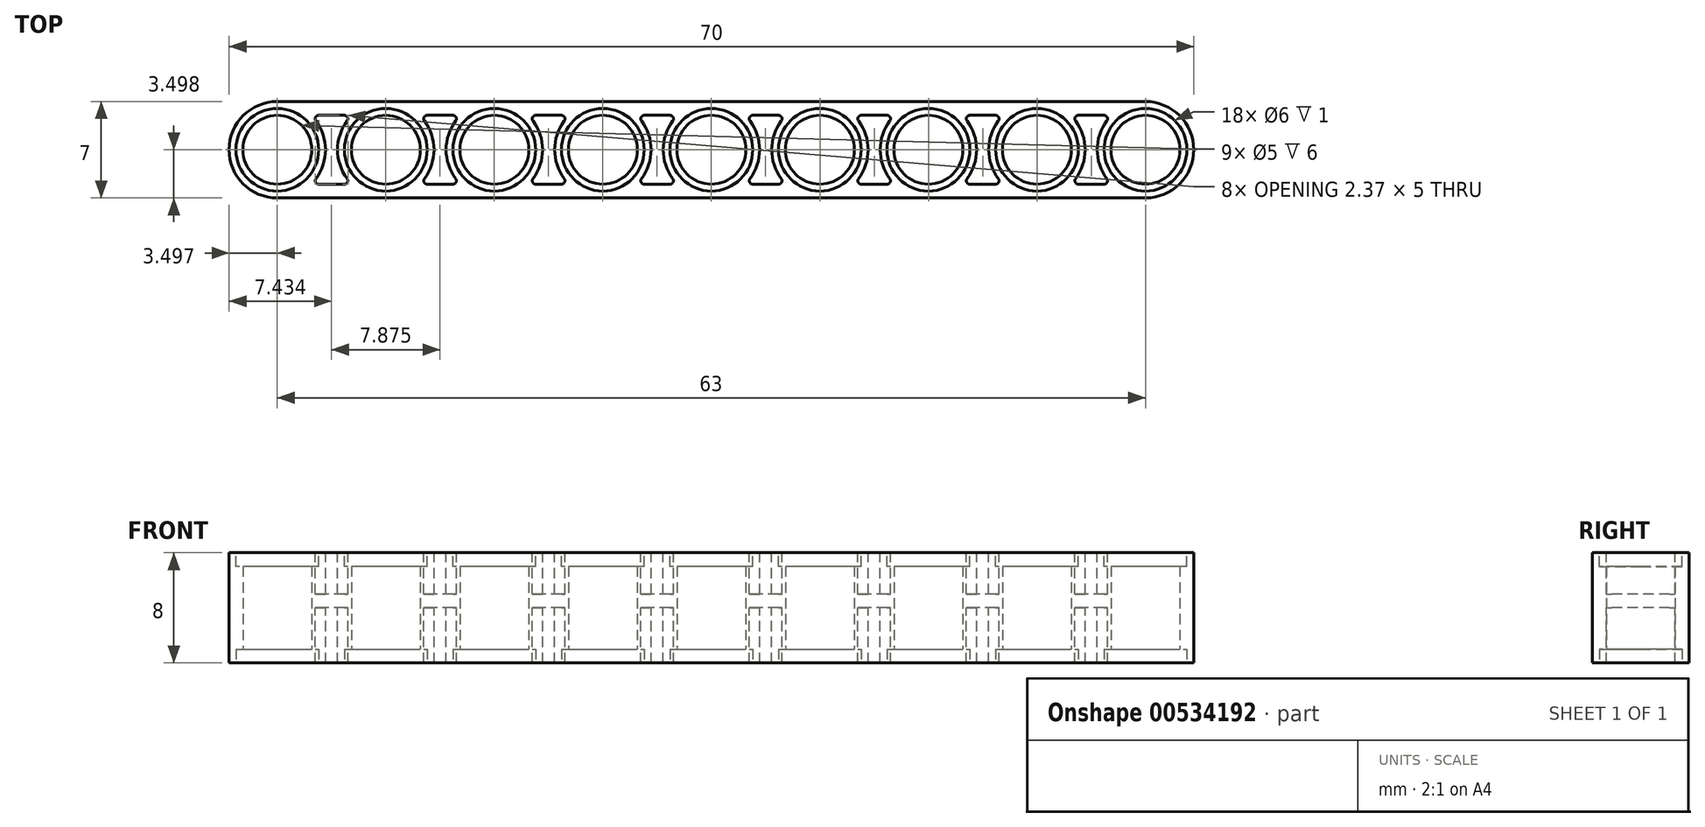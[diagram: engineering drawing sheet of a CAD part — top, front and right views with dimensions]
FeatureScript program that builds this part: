
annotation { "Feature Type Name" : "Feature", "Feature Type Description" : "" }
export const myFeature = defineFeature(function(context is Context, id is Id, definition is map)
    precondition{}
    {
        {
            var Q0;
            Q0=qCreatedBy(makeId("Top.planeOp"),FACE);
            var sketch = newSketch(context, id + "F0", { "sketchPlane" : qUnion([Q0])});
            skCircle(sketch, "E0", {"center": v(-40.67, -41.82) * mm, "radius": 3.5 * mm});
            skLineSegment(sketch, "E1", {"start": v(-40.67, -41.82) * mm, "end": v(22.33, -41.82) * mm});
            skCircle(sketch, "E2", {"center": v(22.33, -41.82) * mm, "radius": 3.5 * mm});
            skLineSegment(sketch, "E3", {"start": v(22.33, -45.32) * mm, "end": v(-40.67, -45.32) * mm});
            skLineSegment(sketch, "E4", {"start": v(-40.67, -38.32) * mm, "end": v(22.33, -38.32) * mm});
            skSolve(sketch);
        }
        {
            var Q0;
            Q0=qSketchRegion(id+"F0",true);
            extrude(context, id + "F1", {"entities" : qUnion([Q0]), "depth" : 8 * mm, "offsetDistance" : 25 * mm});
        }
        {
            var Q0;
            Q0=makeQuery(id+"F1.opExtrude","CAP_FACE",FACE,{"disambiguationData":[OSD([sQuery(id+"F0.wireOp",EDGE,"E0"),sQuery(id+"F0.wireOp",EDGE,"E2"),sQuery(id+"F0.wireOp",EDGE,"E3"),sQuery(id+"F0.wireOp",EDGE,"E4")])],"isStart":true});
            var sketch = newSketch(context, id + "F2", { "sketchPlane" : qUnion([Q0])});
            skArc(sketch, "E5.0", {"start": v(-40.71, -42.4) * mm, "mid": v(-38.21, -39.9) * mm, "end": v(-40.71, -37.4) * mm});
            skArc(sketch, "E5.1", {"start": v(-40.71, -37.4) * mm, "mid": v(-43.21, -39.9) * mm, "end": v(-40.71, -42.4) * mm});
            skCircle(sketch, "E6.0", {"center": v(-40.71, -39.9) * mm, "radius": 3 * mm});
            skLineSegment(sketch, "E7", {"start": v(-38.26, -42.4) * mm, "end": v(-35.16, -42.4) * mm});
            skLineSegment(sketch, "E8", {"start": v(-38.26, -37.4) * mm, "end": v(-35.16, -37.4) * mm});
            skArc(sketch, "E9", {"start": v(-35.16, -37.4) * mm, "mid": v(-36.21, -39.9) * mm, "end": v(-35.16, -42.4) * mm});
            skArc(sketch, "E10", {"start": v(-38.26, -42.4) * mm, "mid": v(-37.21, -39.9) * mm, "end": v(-38.26, -37.4) * mm});
            skCircle(sketch, "E11", {"center": v(-40.67, 41.82) * mm, "radius": 3 * mm});
            skCircle(sketch, "E12", {"center": v(-40.67, 41.82) * mm, "radius": 2.5 * mm});
            skCircle(sketch, "E13.1.0.0", {"center": v(-32.8, 41.82) * mm, "radius": 2.5 * mm});
            skCircle(sketch, "E13.1.0.1", {"center": v(-32.8, 41.82) * mm, "radius": 3 * mm});
            skCircle(sketch, "E13.2.0.0", {"center": v(-24.92, 41.82) * mm, "radius": 2.5 * mm});
            skCircle(sketch, "E13.2.0.1", {"center": v(-24.92, 41.82) * mm, "radius": 3 * mm});
            skCircle(sketch, "E13.3.0.0", {"center": v(-17.05, 41.82) * mm, "radius": 2.5 * mm});
            skCircle(sketch, "E13.3.0.1", {"center": v(-17.05, 41.82) * mm, "radius": 3 * mm});
            skCircle(sketch, "E13.4.0.0", {"center": v(-9.17, 41.82) * mm, "radius": 2.5 * mm});
            skCircle(sketch, "E13.4.0.1", {"center": v(-9.17, 41.82) * mm, "radius": 3 * mm});
            skCircle(sketch, "E13.5.0.0", {"center": v(-1.3, 41.82) * mm, "radius": 2.5 * mm});
            skCircle(sketch, "E13.5.0.1", {"center": v(-1.3, 41.82) * mm, "radius": 3 * mm});
            skCircle(sketch, "E13.6.0.0", {"center": v(6.58, 41.82) * mm, "radius": 2.5 * mm});
            skCircle(sketch, "E13.6.0.1", {"center": v(6.58, 41.82) * mm, "radius": 3 * mm});
            skCircle(sketch, "E13.7.0.0", {"center": v(14.45, 41.82) * mm, "radius": 2.5 * mm});
            skCircle(sketch, "E13.7.0.1", {"center": v(14.45, 41.82) * mm, "radius": 3 * mm});
            skCircle(sketch, "E13.8.0.0", {"center": v(22.33, 41.82) * mm, "radius": 2.5 * mm});
            skCircle(sketch, "E13.8.0.1", {"center": v(22.33, 41.82) * mm, "radius": 3 * mm});
            skLineSegment(sketch, "E13.direction1", {"start": v(-40.67, 41.82) * mm, "end": v(-32.8, 41.82) * mm, "construction": true});
            skSolve(sketch);
        }
        {
            var Q0;
            Q0=makeQuery(id+"F2.imprint","IMPRINT",FACE,{"disambiguationData":[TD([[makeQuery(id+"F2.imprint","IMPRINT",EDGE,{"derivedFrom":sQuery(id+"F2.wireOp",EDGE,"E12")}),1.0]])]});
            var Q1;
            Q1=makeQuery(id+"F2.imprint","IMPRINT",FACE,{"disambiguationData":[TD([[makeQuery(id+"F2.imprint","IMPRINT",EDGE,{"derivedFrom":sQuery(id+"F2.wireOp",EDGE,"E13.1.0.0")}),1.0]])]});
            var Q2;
            Q2=makeQuery(id+"F2.imprint","IMPRINT",FACE,{"disambiguationData":[TD([[makeQuery(id+"F2.imprint","IMPRINT",EDGE,{"derivedFrom":sQuery(id+"F2.wireOp",EDGE,"E13.2.0.0")}),1.0]])]});
            var Q3;
            Q3=makeQuery(id+"F2.imprint","IMPRINT",FACE,{"disambiguationData":[TD([[makeQuery(id+"F2.imprint","IMPRINT",EDGE,{"derivedFrom":sQuery(id+"F2.wireOp",EDGE,"E13.3.0.0")}),1.0]])]});
            var Q4;
            Q4=makeQuery(id+"F2.imprint","IMPRINT",FACE,{"disambiguationData":[TD([[makeQuery(id+"F2.imprint","IMPRINT",EDGE,{"derivedFrom":sQuery(id+"F2.wireOp",EDGE,"E13.4.0.0")}),1.0]])]});
            var Q5;
            Q5=makeQuery(id+"F2.imprint","IMPRINT",FACE,{"disambiguationData":[TD([[makeQuery(id+"F2.imprint","IMPRINT",EDGE,{"derivedFrom":sQuery(id+"F2.wireOp",EDGE,"E13.5.0.0")}),1.0]])]});
            var Q6;
            Q6=makeQuery(id+"F2.imprint","IMPRINT",FACE,{"disambiguationData":[TD([[makeQuery(id+"F2.imprint","IMPRINT",EDGE,{"derivedFrom":sQuery(id+"F2.wireOp",EDGE,"E13.6.0.0")}),1.0]])]});
            var Q7;
            Q7=makeQuery(id+"F2.imprint","IMPRINT",FACE,{"disambiguationData":[TD([[makeQuery(id+"F2.imprint","IMPRINT",EDGE,{"derivedFrom":sQuery(id+"F2.wireOp",EDGE,"E13.7.0.0")}),1.0]])]});
            var Q8;
            Q8=makeQuery(id+"F2.imprint","IMPRINT",FACE,{"disambiguationData":[TD([[makeQuery(id+"F2.imprint","IMPRINT",EDGE,{"derivedFrom":sQuery(id+"F2.wireOp",EDGE,"E13.8.0.0")}),1.0]])]});
            var Q9;
            Q9 = qSketchRegion(id + "F5", true);
            extrude(context, id + "F3", {"entities" : qUnion([Q0, Q1, Q2, Q3, Q4, Q5, Q6, Q7, Q8, Q9]), "operationType" : NewBodyOperationType.REMOVE, "oppositeDirection" : true, "depth" : 25 * mm, "offsetDistance" : 25 * mm});
        }
        {
            var Q0;
            Q0=makeQuery(id+"F2.imprint","IMPRINT",FACE,{"disambiguationData":[TD([[makeQuery(id+"F2.imprint","IMPRINT",EDGE,{"derivedFrom":sQuery(id+"F2.wireOp",EDGE,"E11")}),1.0]])]});
            var Q1;
            Q1=makeQuery(id+"F2.imprint","IMPRINT",FACE,{"disambiguationData":[TD([[makeQuery(id+"F2.imprint","IMPRINT",EDGE,{"derivedFrom":sQuery(id+"F2.wireOp",EDGE,"E13.1.0.0")}),-1.0]])]});
            var Q2;
            Q2=makeQuery(id+"F2.imprint","IMPRINT",FACE,{"disambiguationData":[TD([[makeQuery(id+"F2.imprint","IMPRINT",EDGE,{"derivedFrom":sQuery(id+"F2.wireOp",EDGE,"E13.2.0.0")}),-1.0]])]});
            var Q3;
            Q3=makeQuery(id+"F2.imprint","IMPRINT",FACE,{"disambiguationData":[TD([[makeQuery(id+"F2.imprint","IMPRINT",EDGE,{"derivedFrom":sQuery(id+"F2.wireOp",EDGE,"E13.3.0.0")}),-1.0]])]});
            var Q4;
            Q4=makeQuery(id+"F2.imprint","IMPRINT",FACE,{"disambiguationData":[TD([[makeQuery(id+"F2.imprint","IMPRINT",EDGE,{"derivedFrom":sQuery(id+"F2.wireOp",EDGE,"E13.4.0.0")}),-1.0]])]});
            var Q5;
            Q5=makeQuery(id+"F2.imprint","IMPRINT",FACE,{"disambiguationData":[TD([[makeQuery(id+"F2.imprint","IMPRINT",EDGE,{"derivedFrom":sQuery(id+"F2.wireOp",EDGE,"E13.5.0.0")}),-1.0]])]});
            var Q6;
            Q6=makeQuery(id+"F2.imprint","IMPRINT",FACE,{"disambiguationData":[TD([[makeQuery(id+"F2.imprint","IMPRINT",EDGE,{"derivedFrom":sQuery(id+"F2.wireOp",EDGE,"E13.6.0.0")}),-1.0]])]});
            var Q7;
            Q7=makeQuery(id+"F2.imprint","IMPRINT",FACE,{"disambiguationData":[TD([[makeQuery(id+"F2.imprint","IMPRINT",EDGE,{"derivedFrom":sQuery(id+"F2.wireOp",EDGE,"E13.7.0.0")}),-1.0]])]});
            var Q8;
            Q8=makeQuery(id+"F2.imprint","IMPRINT",FACE,{"disambiguationData":[TD([[makeQuery(id+"F2.imprint","IMPRINT",EDGE,{"derivedFrom":sQuery(id+"F2.wireOp",EDGE,"E13.8.0.0")}),-1.0]])]});
            extrude(context, id + "F4", {"entities" : qUnion([Q0, Q1, Q2, Q3, Q4, Q5, Q6, Q7, Q8]), "operationType" : NewBodyOperationType.REMOVE, "oppositeDirection" : true, "depth" : 1 * mm, "offsetDistance" : 25 * mm});
        }
        {
            var Q0;
            Q0=makeQuery(id+"F1.opExtrude","CAP_FACE",FACE,{"disambiguationData":[OSD([sQuery(id+"F0.wireOp",EDGE,"E0"),sQuery(id+"F0.wireOp",EDGE,"E2"),sQuery(id+"F0.wireOp",EDGE,"E3"),sQuery(id+"F0.wireOp",EDGE,"E4")])],"isStart":false});
            var sketch = newSketch(context, id + "F5", { "sketchPlane" : qUnion([Q0])});
            skCircle(sketch, "E14", {"center": v(22.33, -41.82) * mm, "radius": 3 * mm});
            skCircle(sketch, "E15.1.0.0", {"center": v(14.45, -41.82) * mm, "radius": 3 * mm});
            skCircle(sketch, "E15.2.0.0", {"center": v(6.58, -41.82) * mm, "radius": 3 * mm});
            skCircle(sketch, "E15.3.0.0", {"center": v(-1.3, -41.82) * mm, "radius": 3 * mm});
            skCircle(sketch, "E15.4.0.0", {"center": v(-9.17, -41.82) * mm, "radius": 3 * mm});
            skCircle(sketch, "E15.5.0.0", {"center": v(-17.05, -41.82) * mm, "radius": 3 * mm});
            skCircle(sketch, "E15.6.0.0", {"center": v(-24.92, -41.82) * mm, "radius": 3 * mm});
            skCircle(sketch, "E15.7.0.0", {"center": v(-32.8, -41.82) * mm, "radius": 3 * mm});
            skCircle(sketch, "E15.8.0.0", {"center": v(-40.67, -41.82) * mm, "radius": 3 * mm});
            skLineSegment(sketch, "E15.direction1", {"start": v(22.33, -41.82) * mm, "end": v(14.45, -41.82) * mm, "construction": true});
            skSolve(sketch);
        }
        {
            var Q0;
            Q0=makeQuery(id+"F5.imprint","IMPRINT",FACE,{"disambiguationData":[TD([[makeQuery(id+"F5.imprint","IMPRINT",EDGE,{"derivedFrom":sQuery(id+"F5.wireOp",EDGE,"E14")}),1.0]])]});
            var Q1;
            Q1=makeQuery(id+"F5.imprint","IMPRINT",FACE,{"disambiguationData":[TD([[makeQuery(id+"F5.imprint","IMPRINT",EDGE,{"derivedFrom":sQuery(id+"F5.wireOp",EDGE,"E15.1.0.0")}),1.0]])]});
            var Q2;
            Q2=makeQuery(id+"F5.imprint","IMPRINT",FACE,{"disambiguationData":[TD([[makeQuery(id+"F5.imprint","IMPRINT",EDGE,{"derivedFrom":sQuery(id+"F5.wireOp",EDGE,"E15.2.0.0")}),1.0]])]});
            var Q3;
            Q3=makeQuery(id+"F5.imprint","IMPRINT",FACE,{"disambiguationData":[TD([[makeQuery(id+"F5.imprint","IMPRINT",EDGE,{"derivedFrom":sQuery(id+"F5.wireOp",EDGE,"E15.3.0.0")}),1.0]])]});
            var Q4;
            Q4=makeQuery(id+"F5.imprint","IMPRINT",FACE,{"disambiguationData":[TD([[makeQuery(id+"F5.imprint","IMPRINT",EDGE,{"derivedFrom":sQuery(id+"F5.wireOp",EDGE,"E15.4.0.0")}),1.0]])]});
            var Q5;
            Q5=makeQuery(id+"F5.imprint","IMPRINT",FACE,{"disambiguationData":[TD([[makeQuery(id+"F5.imprint","IMPRINT",EDGE,{"derivedFrom":sQuery(id+"F5.wireOp",EDGE,"E15.5.0.0")}),1.0]])]});
            var Q6;
            Q6=makeQuery(id+"F5.imprint","IMPRINT",FACE,{"disambiguationData":[TD([[makeQuery(id+"F5.imprint","IMPRINT",EDGE,{"derivedFrom":sQuery(id+"F5.wireOp",EDGE,"E15.6.0.0")}),1.0]])]});
            var Q7;
            Q7=makeQuery(id+"F5.imprint","IMPRINT",FACE,{"disambiguationData":[TD([[makeQuery(id+"F5.imprint","IMPRINT",EDGE,{"derivedFrom":sQuery(id+"F5.wireOp",EDGE,"E15.7.0.0")}),1.0]])]});
            var Q8;
            Q8=makeQuery(id+"F5.imprint","IMPRINT",FACE,{"disambiguationData":[TD([[makeQuery(id+"F5.imprint","IMPRINT",EDGE,{"derivedFrom":sQuery(id+"F5.wireOp",EDGE,"E15.8.0.0")}),1.0]])]});
            extrude(context, id + "F6", {"entities" : qUnion([Q0, Q1, Q2, Q3, Q4, Q5, Q6, Q7, Q8]), "operationType" : NewBodyOperationType.REMOVE, "oppositeDirection" : true, "depth" : 1 * mm, "offsetDistance" : 25 * mm});
        }
        {
            var Q0;
            Q0=makeQuery(id+"F1.opExtrude","CAP_FACE",FACE,{"disambiguationData":[OSD([sQuery(id+"F0.wireOp",EDGE,"E0"),sQuery(id+"F0.wireOp",EDGE,"E2"),sQuery(id+"F0.wireOp",EDGE,"E3"),sQuery(id+"F0.wireOp",EDGE,"E4")])],"isStart":false});
            var sketch = newSketch(context, id + "F7", { "sketchPlane" : qUnion([Q0])});
            skArc(sketch, "E16", {"start": v(19.52, -39.73) * mm, "mid": v(18.83, -41.82) * mm, "end": v(19.52, -43.92) * mm});
            skArc(sketch, "E17", {"start": v(17.25, -43.92) * mm, "mid": v(17.95, -41.82) * mm, "end": v(17.25, -39.73) * mm});
            skLineSegment(sketch, "E18", {"start": v(19.32, -44.32) * mm, "end": v(17.46, -44.32) * mm});
            skLineSegment(sketch, "E19", {"start": v(19.32, -39.32) * mm, "end": v(17.46, -39.32) * mm});
            skPoint(sketch, "E20.visualSharp", {"position": v(19.88, -44.32) * mm});
            skArc(sketch, "E20.filletArc", {"start": v(19.32, -44.32) * mm, "mid": v(19.55, -44.18) * mm, "end": v(19.52, -43.92) * mm});
            skPoint(sketch, "E21.visualSharp", {"position": v(16.9, -44.32) * mm});
            skArc(sketch, "E21.filletArc", {"start": v(17.25, -43.92) * mm, "mid": v(17.23, -44.18) * mm, "end": v(17.46, -44.32) * mm});
            skPoint(sketch, "E22.visualSharp", {"position": v(19.88, -39.32) * mm});
            skArc(sketch, "E22.filletArc", {"start": v(19.52, -39.73) * mm, "mid": v(19.55, -39.46) * mm, "end": v(19.32, -39.32) * mm});
            skPoint(sketch, "E23.visualSharp", {"position": v(16.9, -39.32) * mm});
            skArc(sketch, "E23.filletArc", {"start": v(17.46, -39.32) * mm, "mid": v(17.23, -39.46) * mm, "end": v(17.25, -39.73) * mm});
            skArc(sketch, "E24.1.0.0", {"start": v(11.65, -39.73) * mm, "mid": v(10.95, -41.82) * mm, "end": v(11.65, -43.92) * mm});
            skArc(sketch, "E24.1.0.1", {"start": v(9.38, -43.92) * mm, "mid": v(10.08, -41.82) * mm, "end": v(9.38, -39.73) * mm});
            skLineSegment(sketch, "E24.1.0.2", {"start": v(11.45, -44.32) * mm, "end": v(9.58, -44.32) * mm});
            skArc(sketch, "E24.1.0.3", {"start": v(11.45, -44.32) * mm, "mid": v(11.67, -44.18) * mm, "end": v(11.65, -43.92) * mm});
            skArc(sketch, "E24.1.0.4", {"start": v(9.38, -43.92) * mm, "mid": v(9.36, -44.18) * mm, "end": v(9.58, -44.32) * mm});
            skArc(sketch, "E24.1.0.5", {"start": v(9.58, -39.32) * mm, "mid": v(9.36, -39.46) * mm, "end": v(9.38, -39.73) * mm});
            skLineSegment(sketch, "E24.1.0.6", {"start": v(11.45, -39.32) * mm, "end": v(9.58, -39.32) * mm});
            skArc(sketch, "E24.1.0.7", {"start": v(11.65, -39.73) * mm, "mid": v(11.67, -39.46) * mm, "end": v(11.45, -39.32) * mm});
            skArc(sketch, "E24.2.0.0", {"start": v(3.77, -39.73) * mm, "mid": v(3.08, -41.82) * mm, "end": v(3.77, -43.92) * mm});
            skArc(sketch, "E24.2.0.1", {"start": v(1.5, -43.92) * mm, "mid": v(2.2, -41.82) * mm, "end": v(1.5, -39.73) * mm});
            skLineSegment(sketch, "E24.2.0.2", {"start": v(3.57, -44.32) * mm, "end": v(1.7, -44.32) * mm});
            skArc(sketch, "E24.2.0.3", {"start": v(3.57, -44.32) * mm, "mid": v(3.8, -44.18) * mm, "end": v(3.77, -43.92) * mm});
            skArc(sketch, "E24.2.0.4", {"start": v(1.5, -43.92) * mm, "mid": v(1.48, -44.18) * mm, "end": v(1.7, -44.32) * mm});
            skArc(sketch, "E24.2.0.5", {"start": v(1.7, -39.32) * mm, "mid": v(1.48, -39.46) * mm, "end": v(1.5, -39.73) * mm});
            skLineSegment(sketch, "E24.2.0.6", {"start": v(3.57, -39.32) * mm, "end": v(1.7, -39.32) * mm});
            skArc(sketch, "E24.2.0.7", {"start": v(3.77, -39.73) * mm, "mid": v(3.8, -39.46) * mm, "end": v(3.57, -39.32) * mm});
            skArc(sketch, "E24.3.0.0", {"start": v(-4.1, -39.73) * mm, "mid": v(-4.8, -41.82) * mm, "end": v(-4.1, -43.92) * mm});
            skArc(sketch, "E24.3.0.1", {"start": v(-6.37, -43.92) * mm, "mid": v(-5.67, -41.82) * mm, "end": v(-6.37, -39.73) * mm});
            skLineSegment(sketch, "E24.3.0.2", {"start": v(-4.3, -44.32) * mm, "end": v(-6.17, -44.32) * mm});
            skArc(sketch, "E24.3.0.3", {"start": v(-4.3, -44.32) * mm, "mid": v(-4.08, -44.18) * mm, "end": v(-4.1, -43.92) * mm});
            skArc(sketch, "E24.3.0.4", {"start": v(-6.37, -43.92) * mm, "mid": v(-6.4, -44.18) * mm, "end": v(-6.17, -44.32) * mm});
            skArc(sketch, "E24.3.0.5", {"start": v(-6.17, -39.32) * mm, "mid": v(-6.4, -39.46) * mm, "end": v(-6.37, -39.73) * mm});
            skLineSegment(sketch, "E24.3.0.6", {"start": v(-4.3, -39.32) * mm, "end": v(-6.17, -39.32) * mm});
            skArc(sketch, "E24.3.0.7", {"start": v(-4.1, -39.73) * mm, "mid": v(-4.08, -39.46) * mm, "end": v(-4.3, -39.32) * mm});
            skArc(sketch, "E24.4.0.0", {"start": v(-11.98, -39.73) * mm, "mid": v(-12.67, -41.82) * mm, "end": v(-11.98, -43.92) * mm});
            skArc(sketch, "E24.4.0.1", {"start": v(-14.25, -43.92) * mm, "mid": v(-13.55, -41.82) * mm, "end": v(-14.25, -39.73) * mm});
            skLineSegment(sketch, "E24.4.0.2", {"start": v(-12.18, -44.32) * mm, "end": v(-14.04, -44.32) * mm});
            skArc(sketch, "E24.4.0.3", {"start": v(-12.18, -44.32) * mm, "mid": v(-11.95, -44.18) * mm, "end": v(-11.98, -43.92) * mm});
            skArc(sketch, "E24.4.0.4", {"start": v(-14.25, -43.92) * mm, "mid": v(-14.27, -44.18) * mm, "end": v(-14.04, -44.32) * mm});
            skArc(sketch, "E24.4.0.5", {"start": v(-14.04, -39.32) * mm, "mid": v(-14.27, -39.46) * mm, "end": v(-14.25, -39.73) * mm});
            skLineSegment(sketch, "E24.4.0.6", {"start": v(-12.18, -39.32) * mm, "end": v(-14.04, -39.32) * mm});
            skArc(sketch, "E24.4.0.7", {"start": v(-11.98, -39.73) * mm, "mid": v(-11.95, -39.46) * mm, "end": v(-12.18, -39.32) * mm});
            skArc(sketch, "E24.5.0.0", {"start": v(-19.85, -39.73) * mm, "mid": v(-20.55, -41.82) * mm, "end": v(-19.85, -43.92) * mm});
            skArc(sketch, "E24.5.0.1", {"start": v(-22.12, -43.92) * mm, "mid": v(-21.42, -41.82) * mm, "end": v(-22.12, -39.73) * mm});
            skLineSegment(sketch, "E24.5.0.2", {"start": v(-20.05, -44.32) * mm, "end": v(-21.92, -44.32) * mm});
            skArc(sketch, "E24.5.0.3", {"start": v(-20.05, -44.32) * mm, "mid": v(-19.83, -44.18) * mm, "end": v(-19.85, -43.92) * mm});
            skArc(sketch, "E24.5.0.4", {"start": v(-22.12, -43.92) * mm, "mid": v(-22.14, -44.18) * mm, "end": v(-21.92, -44.32) * mm});
            skArc(sketch, "E24.5.0.5", {"start": v(-21.92, -39.32) * mm, "mid": v(-22.14, -39.46) * mm, "end": v(-22.12, -39.73) * mm});
            skLineSegment(sketch, "E24.5.0.6", {"start": v(-20.05, -39.32) * mm, "end": v(-21.92, -39.32) * mm});
            skArc(sketch, "E24.5.0.7", {"start": v(-19.85, -39.73) * mm, "mid": v(-19.83, -39.46) * mm, "end": v(-20.05, -39.32) * mm});
            skArc(sketch, "E24.6.0.0", {"start": v(-27.73, -39.73) * mm, "mid": v(-28.42, -41.82) * mm, "end": v(-27.73, -43.92) * mm});
            skArc(sketch, "E24.6.0.1", {"start": v(-30, -43.92) * mm, "mid": v(-29.3, -41.82) * mm, "end": v(-30, -39.73) * mm});
            skLineSegment(sketch, "E24.6.0.2", {"start": v(-27.93, -44.32) * mm, "end": v(-29.8, -44.32) * mm});
            skArc(sketch, "E24.6.0.3", {"start": v(-27.93, -44.32) * mm, "mid": v(-27.7, -44.18) * mm, "end": v(-27.73, -43.92) * mm});
            skArc(sketch, "E24.6.0.4", {"start": v(-30, -43.92) * mm, "mid": v(-30.02, -44.18) * mm, "end": v(-29.8, -44.32) * mm});
            skArc(sketch, "E24.6.0.5", {"start": v(-29.8, -39.32) * mm, "mid": v(-30.02, -39.46) * mm, "end": v(-30, -39.73) * mm});
            skLineSegment(sketch, "E24.6.0.6", {"start": v(-27.93, -39.32) * mm, "end": v(-29.8, -39.32) * mm});
            skArc(sketch, "E24.6.0.7", {"start": v(-27.73, -39.73) * mm, "mid": v(-27.7, -39.46) * mm, "end": v(-27.93, -39.32) * mm});
            skArc(sketch, "E24.7.0.0", {"start": v(-35.6, -39.73) * mm, "mid": v(-36.3, -41.82) * mm, "end": v(-35.6, -43.92) * mm});
            skArc(sketch, "E24.7.0.1", {"start": v(-37.87, -43.92) * mm, "mid": v(-37.17, -41.82) * mm, "end": v(-37.87, -39.73) * mm});
            skLineSegment(sketch, "E24.7.0.2", {"start": v(-35.8, -44.32) * mm, "end": v(-37.67, -44.32) * mm});
            skArc(sketch, "E24.7.0.3", {"start": v(-35.8, -44.32) * mm, "mid": v(-35.58, -44.18) * mm, "end": v(-35.6, -43.92) * mm});
            skArc(sketch, "E24.7.0.4", {"start": v(-37.87, -43.92) * mm, "mid": v(-37.9, -44.18) * mm, "end": v(-37.67, -44.32) * mm});
            skArc(sketch, "E24.7.0.5", {"start": v(-37.67, -39.32) * mm, "mid": v(-37.9, -39.46) * mm, "end": v(-37.87, -39.73) * mm});
            skLineSegment(sketch, "E24.7.0.6", {"start": v(-35.8, -39.32) * mm, "end": v(-37.67, -39.32) * mm});
            skArc(sketch, "E24.7.0.7", {"start": v(-35.6, -39.73) * mm, "mid": v(-35.58, -39.46) * mm, "end": v(-35.8, -39.32) * mm});
            skLineSegment(sketch, "E24.direction1", {"start": v(14.45, -41.82) * mm, "end": v(6.58, -41.82) * mm, "construction": true});
            skSolve(sketch);
        }
        {
            var Q0;
            Q0=makeQuery(id+"F7.imprint","IMPRINT",FACE,{"disambiguationData":[TD([[makeQuery(id+"F7.imprint","IMPRINT",EDGE,{"derivedFrom":sQuery(id+"F7.wireOp",EDGE,"E16")}),-1.0]])]});
            var Q1;
            Q1=makeQuery(id+"F7.imprint","IMPRINT",FACE,{"disambiguationData":[TD([[makeQuery(id+"F7.imprint","IMPRINT",EDGE,{"derivedFrom":sQuery(id+"F7.wireOp",EDGE,"E24.1.0.0")}),-1.0]])]});
            var Q2;
            Q2=makeQuery(id+"F7.imprint","IMPRINT",FACE,{"disambiguationData":[TD([[makeQuery(id+"F7.imprint","IMPRINT",EDGE,{"derivedFrom":sQuery(id+"F7.wireOp",EDGE,"E24.2.0.0")}),-1.0]])]});
            var Q3;
            Q3=makeQuery(id+"F7.imprint","IMPRINT",FACE,{"disambiguationData":[TD([[makeQuery(id+"F7.imprint","IMPRINT",EDGE,{"derivedFrom":sQuery(id+"F7.wireOp",EDGE,"E24.3.0.0")}),-1.0]])]});
            var Q4;
            Q4=makeQuery(id+"F7.imprint","IMPRINT",FACE,{"disambiguationData":[TD([[makeQuery(id+"F7.imprint","IMPRINT",EDGE,{"derivedFrom":sQuery(id+"F7.wireOp",EDGE,"E24.4.0.0")}),-1.0]])]});
            var Q5;
            Q5=makeQuery(id+"F7.imprint","IMPRINT",FACE,{"disambiguationData":[TD([[makeQuery(id+"F7.imprint","IMPRINT",EDGE,{"derivedFrom":sQuery(id+"F7.wireOp",EDGE,"E24.5.0.0")}),-1.0]])]});
            var Q6;
            Q6=makeQuery(id+"F7.imprint","IMPRINT",FACE,{"disambiguationData":[TD([[makeQuery(id+"F7.imprint","IMPRINT",EDGE,{"derivedFrom":sQuery(id+"F7.wireOp",EDGE,"E24.7.0.0")}),-1.0]])]});
            var Q7;
            Q7=makeQuery(id+"F7.imprint","IMPRINT",FACE,{"disambiguationData":[TD([[makeQuery(id+"F7.imprint","IMPRINT",EDGE,{"derivedFrom":sQuery(id+"F7.wireOp",EDGE,"E24.6.0.0")}),-1.0]])]});
            extrude(context, id + "F8", {"entities" : qUnion([Q0, Q1, Q2, Q3, Q4, Q5, Q6, Q7]), "operationType" : NewBodyOperationType.REMOVE, "oppositeDirection" : true, "depth" : 8 * mm, "offsetDistance" : 25 * mm});
        }
        {
            var Q0;
            Q0=qSketchRegion(id+"F7",true);
            extrude(context, id + "F9", {"entities" : qUnion([Q0]), "operationType" : NewBodyOperationType.ADD, "oppositeDirection" : true, "depth" : 4 * mm, "offsetDistance" : 25 * mm});
        }
        {
            var Q0;
            Q0=qSketchRegion(id+"F7",true);
            extrude(context, id + "F10", {"entities" : qUnion([Q0]), "operationType" : NewBodyOperationType.REMOVE, "oppositeDirection" : true, "depth" : 3 * mm, "offsetDistance" : 25 * mm});
        }
    });
